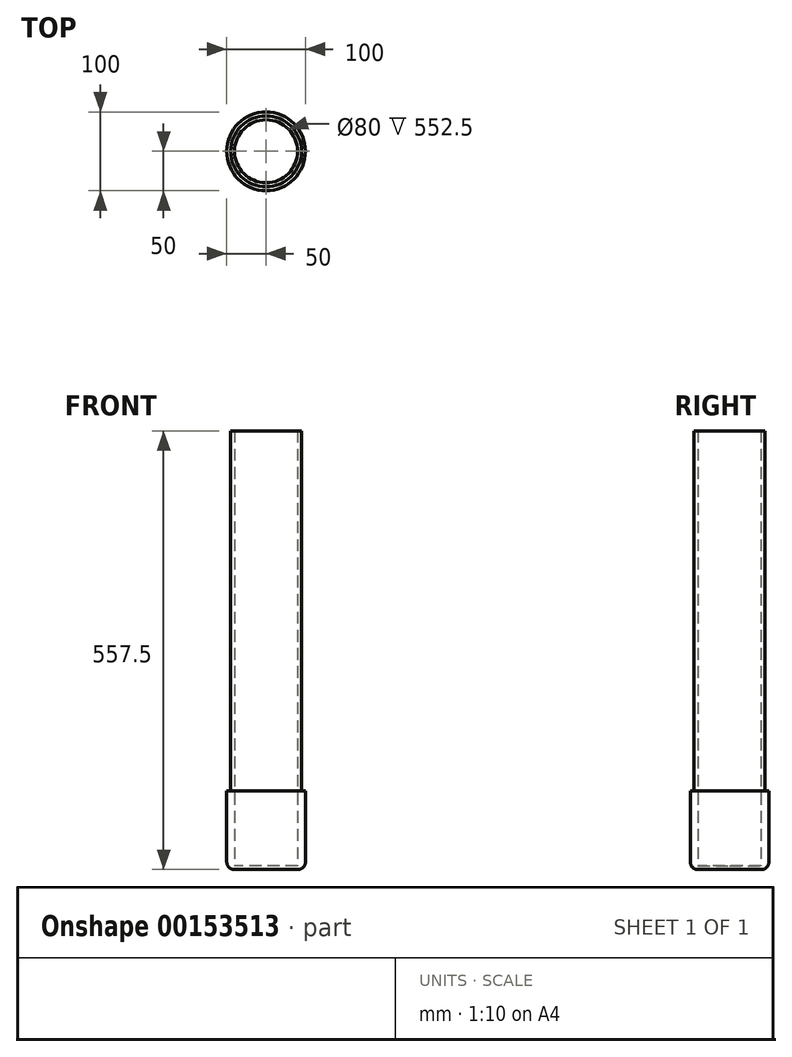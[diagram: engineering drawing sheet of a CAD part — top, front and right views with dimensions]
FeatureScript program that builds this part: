
annotation { "Feature Type Name" : "Feature", "Feature Type Description" : "" }
export const myFeature = defineFeature(function(context is Context, id is Id, definition is map)
    precondition{}
    {
        {
            var Q0;
            Q0=qCreatedBy(makeId("Top.planeOp"),FACE);
            var sketch = newSketch(context, id + "F0", { "sketchPlane" : qUnion([Q0])});
            skCircle(sketch, "E0", {"center": v(0, 0) * mm, "radius": 45 * mm});
            skCircle(sketch, "E1", {"center": v(0, 0) * mm, "radius": 50 * mm});
            skCircle(sketch, "E2", {"center": v(0, 0) * mm, "radius": 40 * mm});
            skSolve(sketch);
        }
        {
            var Q0;
            Q0=makeQuery(id+"F0.imprint","IMPRINT",FACE,{"disambiguationData":[TD([[makeQuery(id+"F0.imprint","IMPRINT",EDGE,{"derivedFrom":sQuery(id+"F0.wireOp",EDGE,"E0")}),1.0]])]});
            extrude(context, id + "F1", {"entities" : qUnion([Q0]), "depth" : 50 * mm});
        }
        {
            var Q0;
            Q0=makeQuery(id+"F0.imprint","IMPRINT",FACE,{"disambiguationData":[TD([[makeQuery(id+"F0.imprint","IMPRINT",EDGE,{"derivedFrom":sQuery(id+"F0.wireOp",EDGE,"E0")}),-1.0]])]});
            extrude(context, id + "F2", {"entities" : qUnion([Q0]), "operationType" : NewBodyOperationType.ADD, "depth" : 100 * mm});
        }
        {
            var Q0;
            Q0=makeQuery(id+"F0.imprint","IMPRINT",FACE,{"disambiguationData":[TD([[makeQuery(id+"F0.imprint","IMPRINT",EDGE,{"derivedFrom":sQuery(id+"F0.wireOp",EDGE,"E2")}),1.0]])]});
            var Q1;
            Q1=makeQuery(id+"F0.imprint","IMPRINT",FACE,{"disambiguationData":[TD([[makeQuery(id+"F0.imprint","IMPRINT",EDGE,{"derivedFrom":sQuery(id+"F0.wireOp",EDGE,"E0")}),1.0]])]});
            var Q2;
            Q2=makeQuery(id+"F0.imprint","IMPRINT",FACE,{"disambiguationData":[TD([[makeQuery(id+"F0.imprint","IMPRINT",EDGE,{"derivedFrom":sQuery(id+"F0.wireOp",EDGE,"E0")}),-1.0]])]});
            extrude(context, id + "F3", {"entities" : qUnion([Q0, Q1, Q2]), "operationType" : NewBodyOperationType.ADD, "depth" : 5 * mm});
        }
        {
            var Q0;
            Q0=makeQuery(id+"F2.opExtrude","CAP_EDGE",EDGE,{"disambiguationData":[OSD([sQuery(id+"F0.wireOp",EDGE,"E1")])],"isStart":true});
            fillet(context, id + "F4", {"entities" : qUnion([Q0]), "radius" : 10 * mm, "tangentPropagation" : true, "allowEdgeOverflow" : false});
        }
        {
            var Q0;
            Q0=makeQuery(id+"F1.opExtrude","CAP_FACE",FACE,{"disambiguationData":[OSD([sQuery(id+"F0.wireOp",EDGE,"E0"),sQuery(id+"F0.wireOp",EDGE,"E2")])],"isStart":false});
            extrude(context, id + "F5", {"entities" : qUnion([Q0]), "operationType" : NewBodyOperationType.ADD, "depth" : 507.5 * mm});
        }
    });
